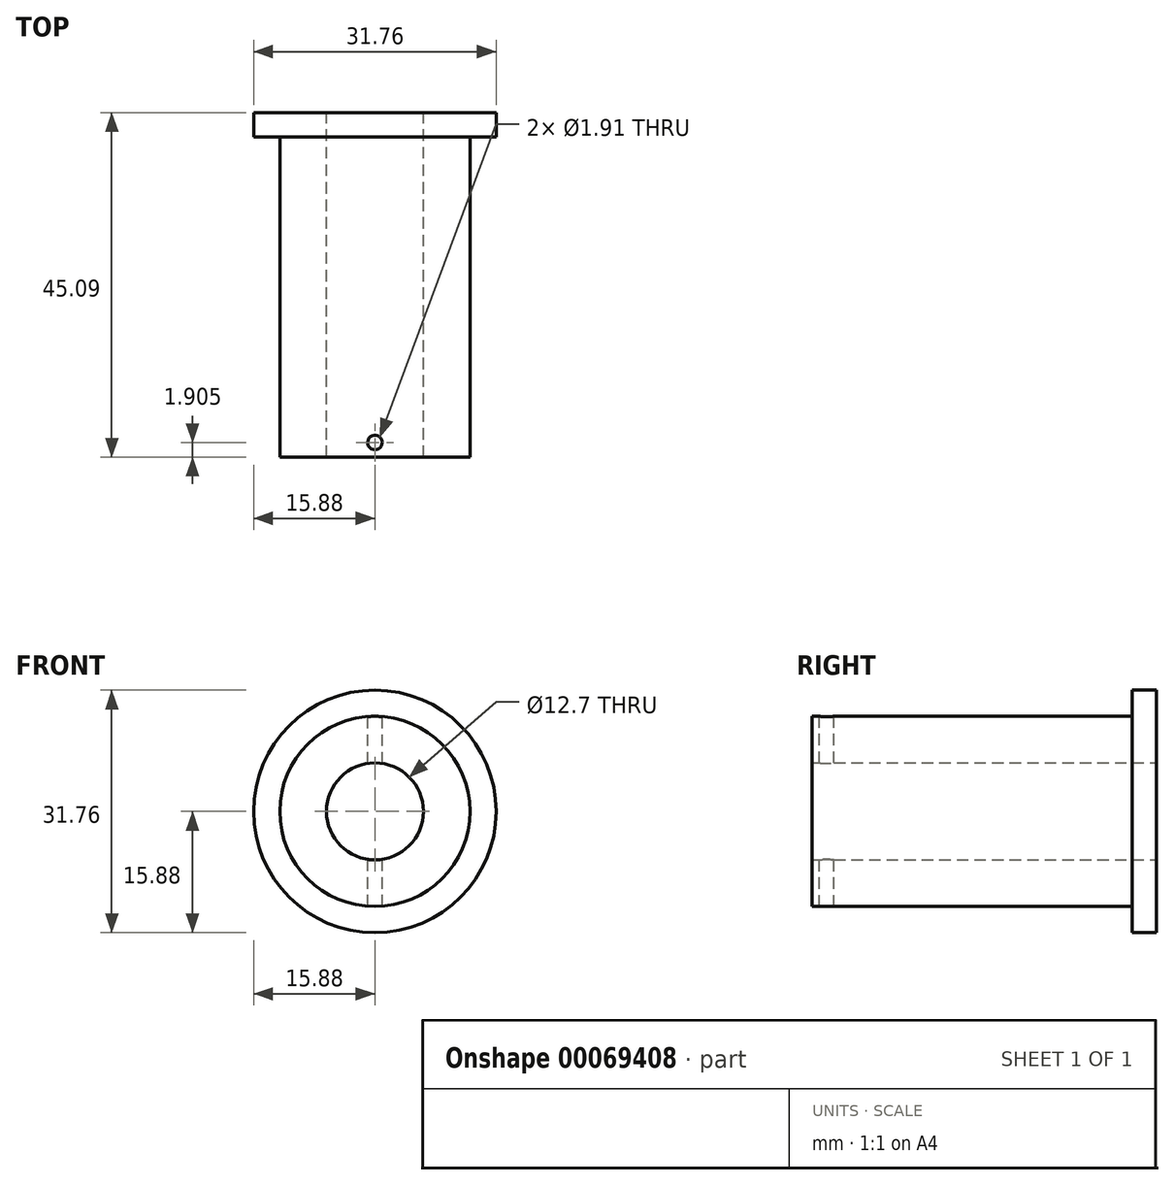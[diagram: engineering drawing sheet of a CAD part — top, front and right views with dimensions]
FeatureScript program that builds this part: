
annotation { "Feature Type Name" : "Feature", "Feature Type Description" : "" }
export const myFeature = defineFeature(function(context is Context, id is Id, definition is map)
    precondition{}
    {
        {
            var Q0;
            Q0=qCreatedBy(makeId("Front.planeOp"),FACE);
            var sketch = newSketch(context, id + "F0", { "sketchPlane" : qUnion([Q0])});
            skCircle(sketch, "E0", {"center": v(0, 0) * mm, "radius": 12.45 * mm});
            skCircle(sketch, "E1", {"center": v(0, 0) * mm, "radius": 6.35 * mm});
            skSolve(sketch);
        }
        {
            var Q0;
            Q0=makeQuery(id+"F0.imprint","IMPRINT",FACE,{"disambiguationData":[TD([[makeQuery(id+"F0.imprint","IMPRINT",EDGE,{"derivedFrom":sQuery(id+"F0.wireOp",EDGE,"E0")}),1.0]])]});
            extrude(context, id + "F1", {"entities" : qUnion([Q0]), "depth" : 41.9 * mm});
        }
        {
            var Q0;
            Q0=qCreatedBy(makeId("Front.planeOp"),FACE);
            var sketch = newSketch(context, id + "F2", { "sketchPlane" : qUnion([Q0])});
            skCircle(sketch, "E2", {"center": v(0, 0) * mm, "radius": 6.35 * mm});
            skCircle(sketch, "E3", {"center": v(0, 0) * mm, "radius": 15.88 * mm});
            skSolve(sketch);
        }
        {
            var Q0;
            Q0=makeQuery(id+"F2.imprint","IMPRINT",FACE,{"disambiguationData":[TD([[makeQuery(id+"F2.imprint","IMPRINT",EDGE,{"derivedFrom":sQuery(id+"F2.wireOp",EDGE,"E2")}),-1.0]])]});
            extrude(context, id + "F3", {"entities" : qUnion([Q0]), "operationType" : NewBodyOperationType.ADD, "oppositeDirection" : true, "depth" : 3.17 * mm});
        }
        {
            var Q0;
            Q0=qCreatedBy(makeId("Top.planeOp"),FACE);
            cPlane(context, id + "F4", {"entities" : qUnion([Q0]), "cplaneType" : CPlaneType.OFFSET, "offset" : 25.4 * mm, "width" : 152.4 * mm, "height" : 152.4 * mm});
        }
        {
            var Q0;
            Q0=qCreatedBy(id+"F4.planeOp",FACE);
            var sketch = newSketch(context, id + "F5", { "sketchPlane" : qUnion([Q0])});
            skLineSegment(sketch, "E4", {"start": v(12.45, 0) * mm, "end": v(12.45, -38.1) * mm});
            skLineSegment(sketch, "E5", {"start": v(-12.45, -38.1) * mm, "end": v(-12.45, 0) * mm});
            skCircle(sketch, "E6", {"center": v(0, -40) * mm, "radius": 0.95 * mm});
            skSolve(sketch);
        }
        {
            var Q0;
            Q0=makeQuery(id+"F5.imprint","IMPRINT",FACE,{"disambiguationData":[TD([[makeQuery(id+"F5.imprint","IMPRINT",EDGE,{"derivedFrom":sQuery(id+"F5.wireOp",EDGE,"E6")}),1.0]])]});
            extrude(context, id + "F6", {"entities" : qUnion([Q0]), "operationType" : NewBodyOperationType.REMOVE, "endBound" : BoundingType.THROUGH_ALL, "oppositeDirection" : true, "depth" : 25.4 * mm});
        }
    });
